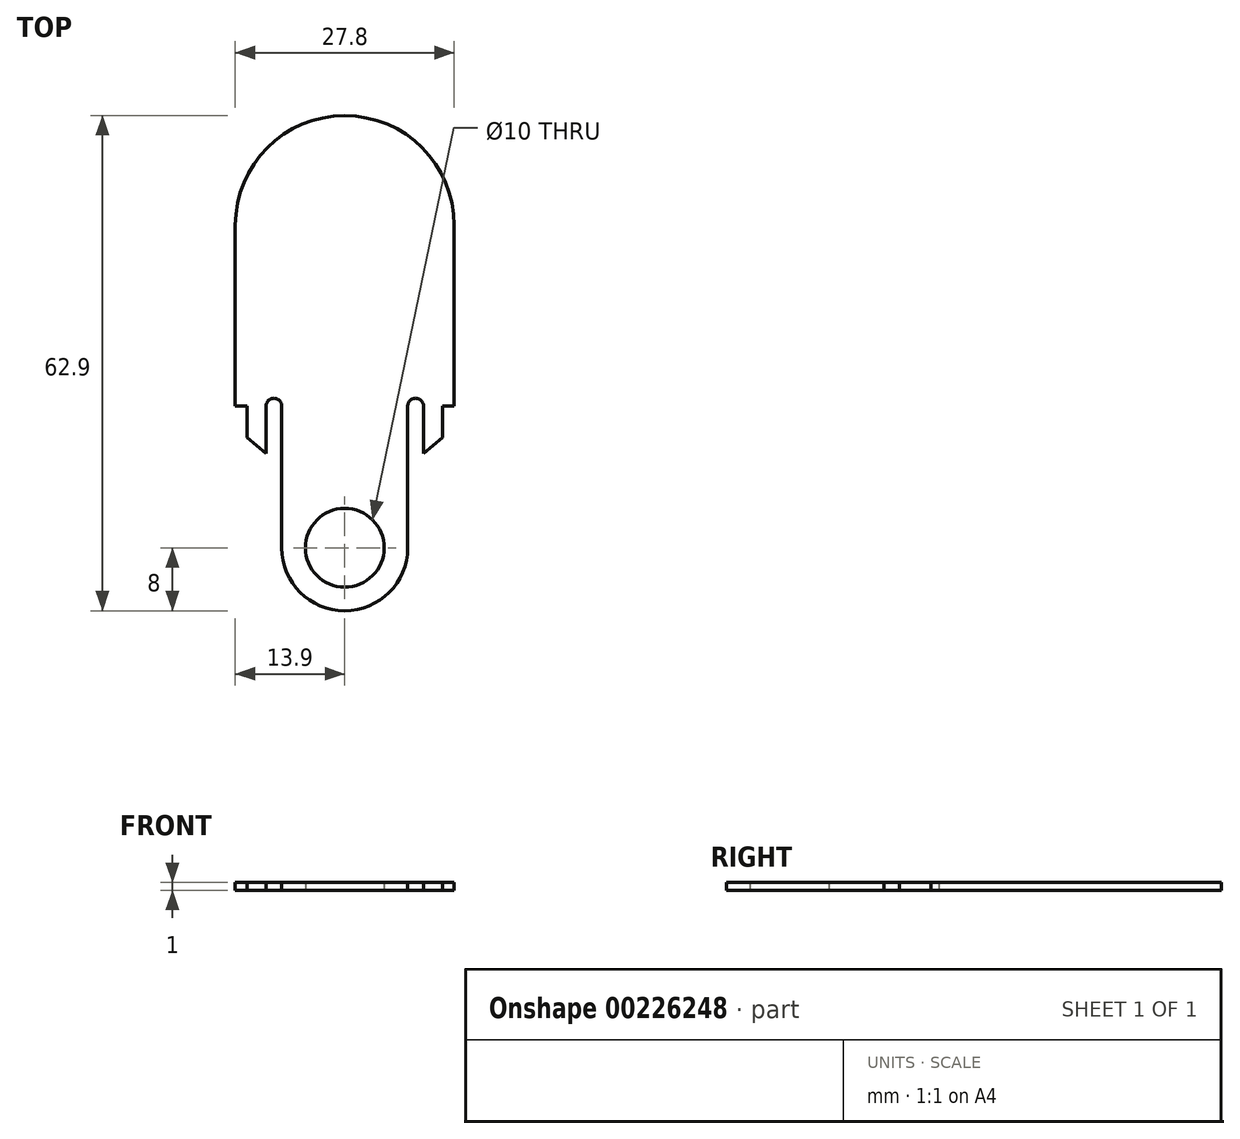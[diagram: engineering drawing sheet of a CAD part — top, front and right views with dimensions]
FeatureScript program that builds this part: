
annotation { "Feature Type Name" : "Feature", "Feature Type Description" : "" }
export const myFeature = defineFeature(function(context is Context, id is Id, definition is map)
    precondition{}
    {
        {
            var Q0;
            Q0=qCreatedBy(makeId("Top.planeOp"),FACE);
            var sketch = newSketch(context, id + "F0", { "sketchPlane" : qUnion([Q0])});
            skLineSegment(sketch, "E0", {"start": v(-10, -29) * mm, "end": v(-12.4, -27) * mm});
            skLineSegment(sketch, "E1", {"start": v(-12.4, -27) * mm, "end": v(-12.4, -23) * mm});
            skLineSegment(sketch, "E2", {"start": v(-12.4, -23) * mm, "end": v(-13.9, -23) * mm});
            skLineSegment(sketch, "E3", {"start": v(-13.9, -23) * mm, "end": v(-13.9, 0) * mm});
            skArc(sketch, "E4", {"start": v(13.9, 0) * mm, "mid": v(0, 13.9) * mm, "end": v(-13.9, 0) * mm});
            skLineSegment(sketch, "E5", {"start": v(13.9, 0) * mm, "end": v(13.9, -23) * mm});
            skLineSegment(sketch, "E6", {"start": v(13.9, -23) * mm, "end": v(12.4, -23) * mm});
            skLineSegment(sketch, "E7", {"start": v(12.4, -23) * mm, "end": v(12.4, -27) * mm});
            skLineSegment(sketch, "E8", {"start": v(12.4, -27) * mm, "end": v(10, -29) * mm});
            skLineSegment(sketch, "E9", {"start": v(10, -29) * mm, "end": v(10, -23) * mm});
            skArc(sketch, "E10", {"start": v(10, -23) * mm, "mid": v(9, -22) * mm, "end": v(8, -23) * mm});
            skLineSegment(sketch, "E11", {"start": v(8, -23) * mm, "end": v(8, -41) * mm});
            skArc(sketch, "E12", {"start": v(-8, -41) * mm, "mid": v(0, -49) * mm, "end": v(8, -41) * mm});
            skLineSegment(sketch, "E13", {"start": v(-8, -41) * mm, "end": v(-8, -23) * mm});
            skArc(sketch, "E14", {"start": v(-8, -23) * mm, "mid": v(-9, -22) * mm, "end": v(-10, -23) * mm});
            skLineSegment(sketch, "E15", {"start": v(-10, -23) * mm, "end": v(-10, -29) * mm});
            skCircle(sketch, "E16", {"center": v(0, -41) * mm, "radius": 5 * mm});
            skSolve(sketch);
        }
        {
            var Q0;
            Q0 = qSketchRegion(id + "F0", true);
            extrude(context, id + "F1", {"entities" : qUnion([Q0]), "depth" : 1 * mm});
        }
    });
